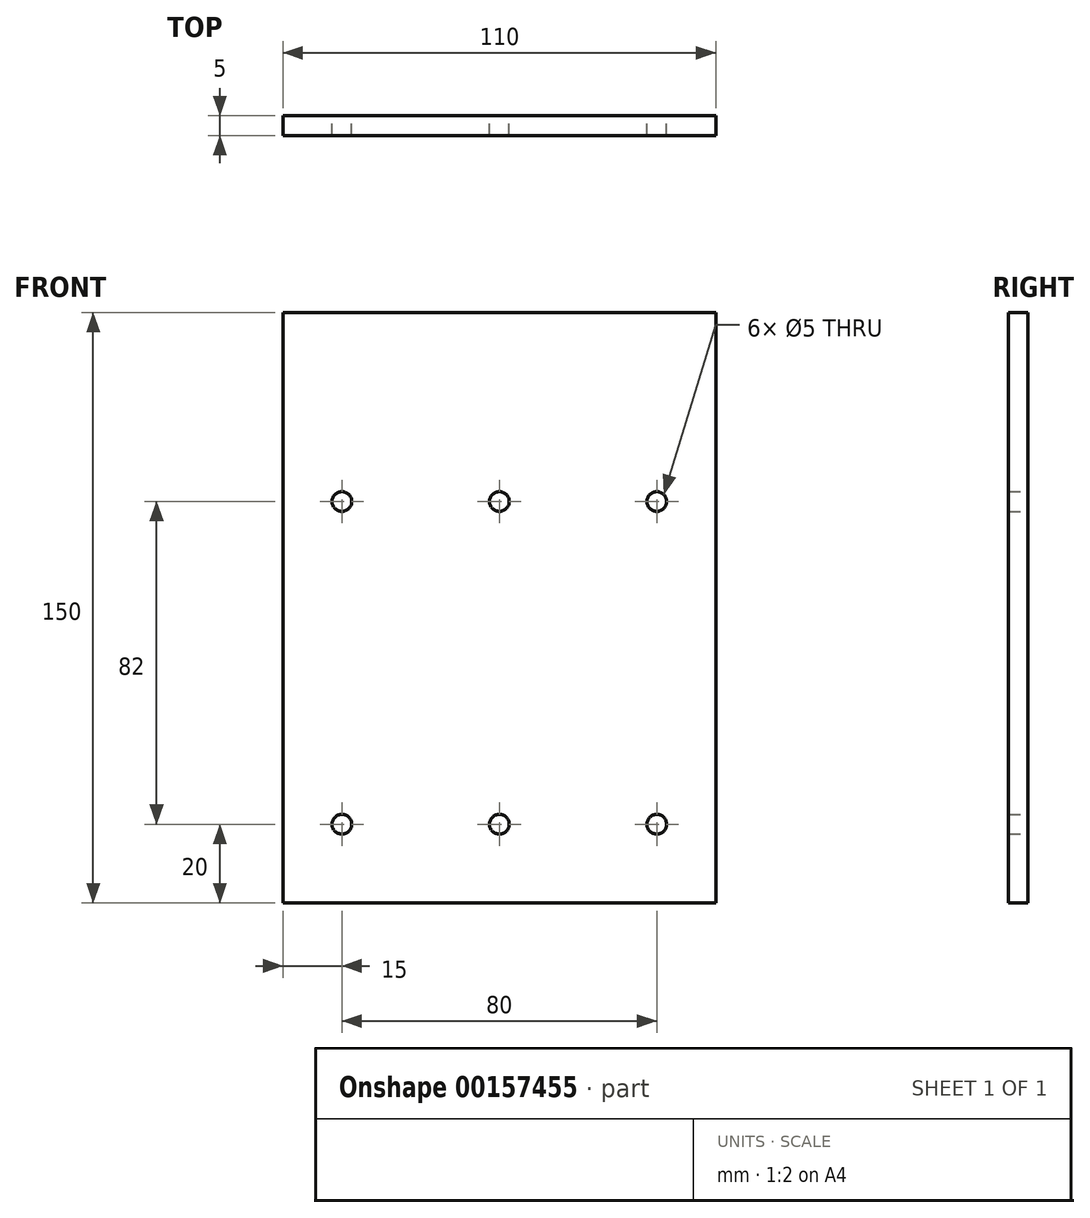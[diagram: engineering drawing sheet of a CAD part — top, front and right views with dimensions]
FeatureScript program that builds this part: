
annotation { "Feature Type Name" : "Feature", "Feature Type Description" : "" }
export const myFeature = defineFeature(function(context is Context, id is Id, definition is map)
    precondition{}
    {
        {
            var Q0;
            Q0=qCreatedBy(makeId("Front.planeOp"),FACE);
            var sketch = newSketch(context, id + "F0", { "sketchPlane" : qUnion([Q0])});
            skLineSegment(sketch, "E0.bottom", {"start": v(55, -75) * mm, "end": v(-55, -75) * mm});
            skLineSegment(sketch, "E0.top", {"start": v(55, 75) * mm, "end": v(0, 75) * mm});
            skLineSegment(sketch, "E0.left", {"start": v(55, -75) * mm, "end": v(55, 75) * mm});
            skLineSegment(sketch, "E0.right", {"start": v(-55, -75) * mm, "end": v(-55, 38.3) * mm});
            skPoint(sketch, "E0.middle", {"position": v(0, 0) * mm});
            skCircle(sketch, "E1", {"center": v(-40, 27) * mm, "radius": 2.5 * mm});
            skCircle(sketch, "E2", {"center": v(0, 27) * mm, "radius": 2.5 * mm});
            skCircle(sketch, "E3", {"center": v(-40, -55) * mm, "radius": 2.5 * mm});
            skCircle(sketch, "E4", {"center": v(0, -55) * mm, "radius": 2.5 * mm});
            skCircle(sketch, "E5", {"center": v(40, -55) * mm, "radius": 2.5 * mm});
            skCircle(sketch, "E6", {"center": v(40, 27) * mm, "radius": 2.5 * mm});
            skPoint(sketch, "E7.orphan", {"position": v(-55, 75) * mm});
            skLineSegment(sketch, "E8", {"start": v(0, 75) * mm, "end": v(-55, 75) * mm});
            skLineSegment(sketch, "E9", {"start": v(-55, 75) * mm, "end": v(-55, 38.3) * mm});
            skSolve(sketch);
        }
        {
            var Q0;
            Q0=makeQuery(id+"F0.imprint","IMPRINT",FACE,{"disambiguationData":[TD([[makeQuery(id+"F0.imprint","IMPRINT",EDGE,{"derivedFrom":sQuery(id+"F0.wireOp",EDGE,"E0.bottom")}),-1.0]])]});
            extrude(context, id + "F1", {"entities" : qUnion([Q0]), "depth" : 5 * mm});
        }
    });
